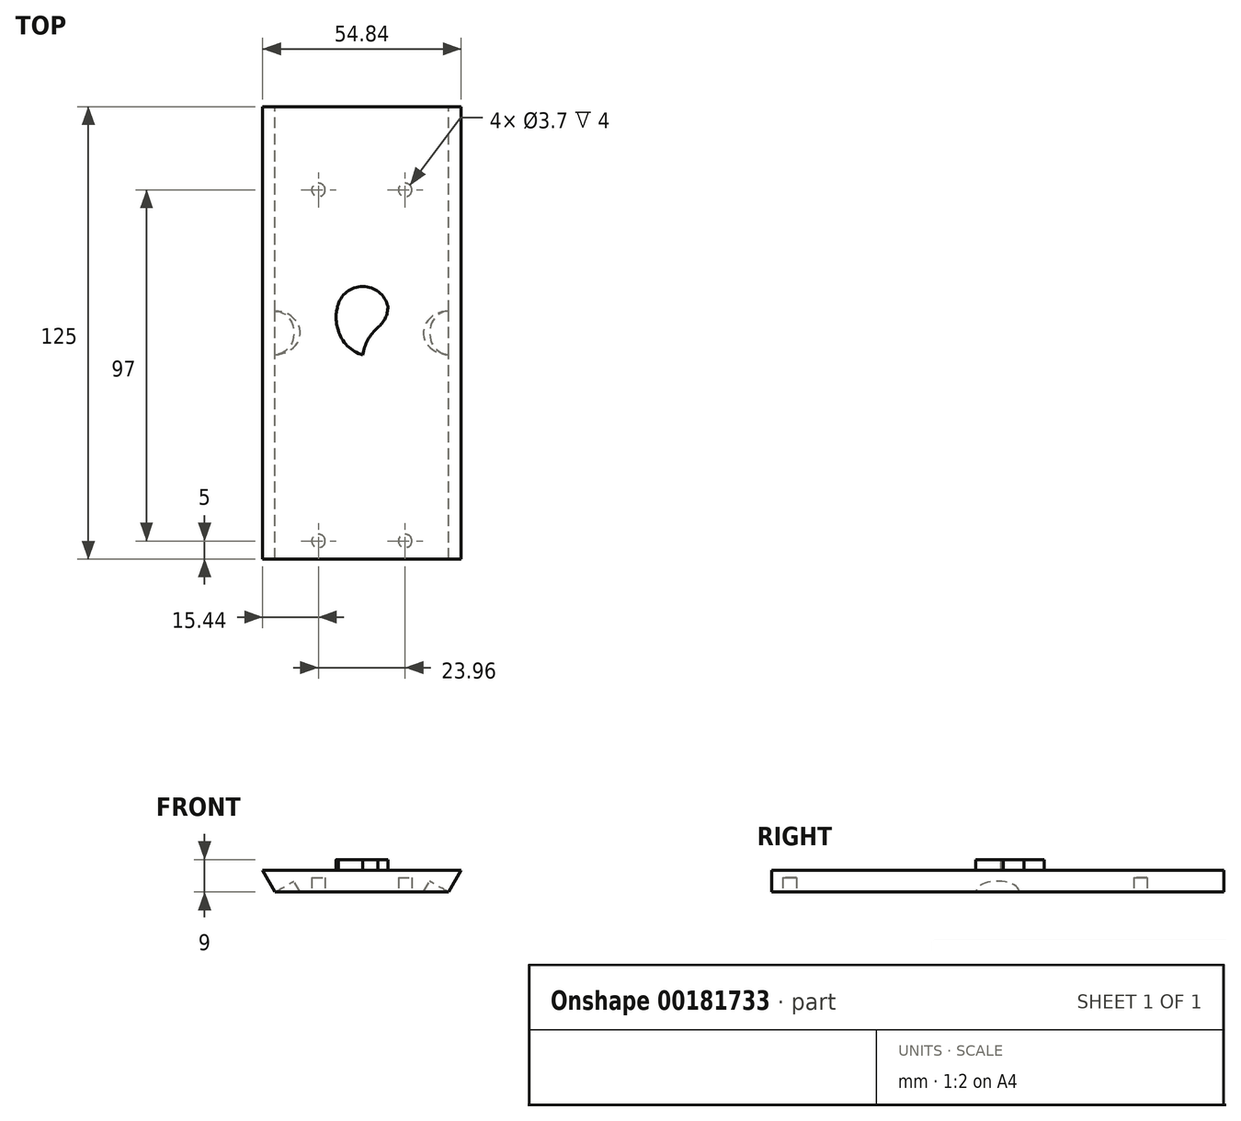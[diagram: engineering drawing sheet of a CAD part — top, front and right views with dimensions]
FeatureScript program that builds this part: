
annotation { "Feature Type Name" : "Feature", "Feature Type Description" : "" }
export const myFeature = defineFeature(function(context is Context, id is Id, definition is map)
    precondition{}
    {
        {
            var Q0;
            Q0=qCreatedBy(makeId("Front.planeOp"),FACE);
            var sketch = newSketch(context, id + "F0", { "sketchPlane" : qUnion([Q0])});
            skCircle(sketch, "E0.cCircle", {"center": v(0, 0) * mm, "radius": 47.5 * mm, "construction": true});
            skLineSegment(sketch, "E0.0", {"start": v(-27.42, -47.5) * mm, "end": v(-54.85, 0) * mm});
            skLineSegment(sketch, "E0.1", {"start": v(-54.85, 0) * mm, "end": v(-27.42, 47.5) * mm});
            skLineSegment(sketch, "E0.2", {"start": v(-27.42, 47.5) * mm, "end": v(27.42, 47.5) * mm});
            skLineSegment(sketch, "E0.3", {"start": v(27.42, 47.5) * mm, "end": v(54.85, 0) * mm});
            skLineSegment(sketch, "E0.4", {"start": v(54.85, 0) * mm, "end": v(27.42, -47.5) * mm});
            skLineSegment(sketch, "E0.5", {"start": v(27.42, -47.5) * mm, "end": v(-27.42, -47.5) * mm});
            skPoint(sketch, "E0.0.midPoint", {"position": v(-41.14, -23.75) * mm});
            skCircle(sketch, "E1.cCircle", {"center": v(0, 0) * mm, "radius": 41.5 * mm, "construction": true});
            skLineSegment(sketch, "E1.0", {"start": v(-23.96, -41.5) * mm, "end": v(-47.92, 0) * mm});
            skLineSegment(sketch, "E1.1", {"start": v(-47.92, 0) * mm, "end": v(-23.96, 41.5) * mm});
            skLineSegment(sketch, "E1.2", {"start": v(-23.96, 41.5) * mm, "end": v(23.96, 41.5) * mm});
            skLineSegment(sketch, "E1.3", {"start": v(23.96, 41.5) * mm, "end": v(47.92, 0) * mm});
            skLineSegment(sketch, "E1.4", {"start": v(47.92, 0) * mm, "end": v(23.96, -41.5) * mm});
            skLineSegment(sketch, "E1.5", {"start": v(23.96, -41.5) * mm, "end": v(-23.96, -41.5) * mm});
            skPoint(sketch, "E1.0.midPoint", {"position": v(-35.94, -20.75) * mm});
            skLineSegment(sketch, "E2", {"start": v(27.42, 47.5) * mm, "end": v(23.96, 41.5) * mm});
            skLineSegment(sketch, "E3", {"start": v(-27.42, 47.5) * mm, "end": v(-23.96, 41.5) * mm});
            skSolve(sketch);
        }
        {
            var Q0;
            Q0=makeQuery(id+"F0.imprint","IMPRINT",FACE,{"disambiguationData":[TD([[makeQuery(id+"F0.imprint","IMPRINT",EDGE,{"derivedFrom":sQuery(id+"F0.wireOp",EDGE,"E0.2")}),-1.0]])]});
            extrude(context, id + "F1", {"entities" : qUnion([Q0]), "depth" : 125 * mm});
        }
        {
            var Q0;
            Q0=makeQuery(id+"F1.opExtrude","SWEPT_FACE",FACE,{"disambiguationData":[OSD([sQuery(id+"F0.wireOp",EDGE,"E1.2")])]});
            var sketch = newSketch(context, id + "F2", { "sketchPlane" : qUnion([Q0])});
            skPoint(sketch, "E4", {"position": v(0, 125) * mm});
            skPoint(sketch, "E5", {"position": v(0, 120) * mm});
            skLineSegment(sketch, "E6", {"start": v(0, 120) * mm, "end": v(-23.96, 120) * mm});
            skPoint(sketch, "E7", {"position": v(-11.98, 120) * mm});
            skCircle(sketch, "E8", {"center": v(-11.98, 120) * mm, "radius": 1.85 * mm});
            skCircle(sketch, "E9.MirrorC", {"center": v(11.98, 120) * mm, "radius": 1.85 * mm});
            skPoint(sketch, "E10", {"position": v(0, 23) * mm});
            skLineSegment(sketch, "E11", {"start": v(0, 23) * mm, "end": v(-23.96, 23) * mm});
            skPoint(sketch, "E12", {"position": v(-11.98, 23) * mm});
            skCircle(sketch, "E13", {"center": v(-11.98, 23) * mm, "radius": 1.85 * mm});
            skCircle(sketch, "E14.MirrorC", {"center": v(11.98, 23) * mm, "radius": 1.85 * mm});
            skSolve(sketch);
        }
        {
            var Q0;
            Q0 = qSketchRegion(id + "F2", true);
            extrude(context, id + "F3", {"entities" : qUnion([Q0]), "operationType" : NewBodyOperationType.REMOVE, "oppositeDirection" : true, "depth" : 4 * mm});
        }
        {
            var Q0;
            Q0=makeQuery(id+"F1.opExtrude","SWEPT_FACE",FACE,{"disambiguationData":[OSD([sQuery(id+"F0.wireOp",EDGE,"E0.2")])]});
            var sketch = newSketch(context, id + "F4", { "sketchPlane" : qUnion([Q0])});
            skPoint(sketch, "E15", {"position": v(-23.96, -62.5) * mm});
            skPoint(sketch, "E16", {"position": v(0, -62.5) * mm});
            skPoint(sketch, "E17", {"position": v(0, -90) * mm});
            skArc(sketch, "E18.MirrorCS", {"start": v(7.17, -55.21) * mm, "mid": v(0.24, -49.68) * mm, "end": v(-6.68, -55.21) * mm});
            skArc(sketch, "E19.MirrorCS", {"start": v(4.42, -61) * mm, "mid": v(6.48, -58.43) * mm, "end": v(7.17, -55.21) * mm});
            skArc(sketch, "E20.MirrorCS", {"start": v(4.42, -61) * mm, "mid": v(1.66, -64.44) * mm, "end": v(0.24, -68.6) * mm});
            skArc(sketch, "E21.MirrorCS", {"start": v(-6.5, -61.75) * mm, "mid": v(-4.03, -66.07) * mm, "end": v(0.24, -68.6) * mm});
            skArc(sketch, "E22.MirrorCS", {"start": v(-6.68, -55.21) * mm, "mid": v(-7.1, -58.5) * mm, "end": v(-6.5, -61.75) * mm});
            skLineSegment(sketch, "E23.MirrorCS", {"start": v(-9.75, -69.44) * mm, "end": v(-9.75, -49.44) * mm});
            skLineSegment(sketch, "E24.MirrorCS", {"start": v(10.25, -49.44) * mm, "end": v(-9.75, -49.44) * mm});
            skLineSegment(sketch, "E25.MirrorCS", {"start": v(10.25, -69.44) * mm, "end": v(10.25, -49.44) * mm});
            skLineSegment(sketch, "E26.MirrorCS", {"start": v(10.25, -69.44) * mm, "end": v(-9.75, -69.44) * mm});
            skSolve(sketch);
        }
        {
            var Q0;
            Q0=makeQuery(id+"F4.imprint","IMPRINT",FACE,{"disambiguationData":[TD([[makeQuery(id+"F4.imprint","IMPRINT",EDGE,{"derivedFrom":sQuery(id+"F4.wireOp",EDGE,"E18.MirrorCS")}),1.0]])]});
            extrude(context, id + "F5", {"entities" : qUnion([Q0]), "operationType" : NewBodyOperationType.ADD, "depth" : 3 * mm});
        }
        {
            var Q0;
            Q0=makeQuery(id+"F1.opExtrude","SWEPT_EDGE",EDGE,{"disambiguationData":[OSD([sQuery(id+"F0.wireOp",EDGE,"E1.1"),sQuery(id+"F0.wireOp",EDGE,"E1.2"),sQuery(id+"F0.wireOp",EDGE,"E3")])]});
            cPlane(context, id + "F6", {"entities" : qUnion([Q0]), "cplaneType" : CPlaneType.LINE_ANGLE, "offset" : 25 * mm, "angle" : 150 * degree, "width" : 150 * mm, "height" : 150 * mm});
        }
        {
            var Q0;
            Q0=qCreatedBy(id+"F6.planeOp",FACE);
            var sketch = newSketch(context, id + "F7", { "sketchPlane" : qUnion([Q0])});
            skCircle(sketch, "E27", {"center": v(0, 62.5) * mm, "radius": 6 * mm});
            skSolve(sketch);
        }
        {
            var Q0;
            Q0 = qSketchRegion(id + "F7", true);
            extrude(context, id + "F8", {"entities" : qUnion([Q0]), "operationType" : NewBodyOperationType.REMOVE, "depth" : 25 * mm});
        }
        {
            var Q0;
            Q0=makeQuery(id+"F1.opExtrude","SWEPT_EDGE",EDGE,{"disambiguationData":[OSD([sQuery(id+"F0.wireOp",EDGE,"E1.2"),sQuery(id+"F0.wireOp",EDGE,"E1.3"),sQuery(id+"F0.wireOp",EDGE,"E2")])]});
            cPlane(context, id + "F9", {"entities" : qUnion([Q0]), "cplaneType" : CPlaneType.LINE_ANGLE, "offset" : 25 * mm, "angle" : 30 * degree, "width" : 150 * mm, "height" : 150 * mm});
        }
        {
            var Q0;
            Q0=qCreatedBy(id+"F9.planeOp",FACE);
            var sketch = newSketch(context, id + "F10", { "sketchPlane" : qUnion([Q0])});
            skCircle(sketch, "E28", {"center": v(0, -62.5) * mm, "radius": 6 * mm});
            skSolve(sketch);
        }
        {
            var Q0;
            Q0 = qSketchRegion(id + "F10", true);
            extrude(context, id + "F11", {"entities" : qUnion([Q0]), "operationType" : NewBodyOperationType.REMOVE, "oppositeDirection" : true, "depth" : 25 * mm});
        }
    });
